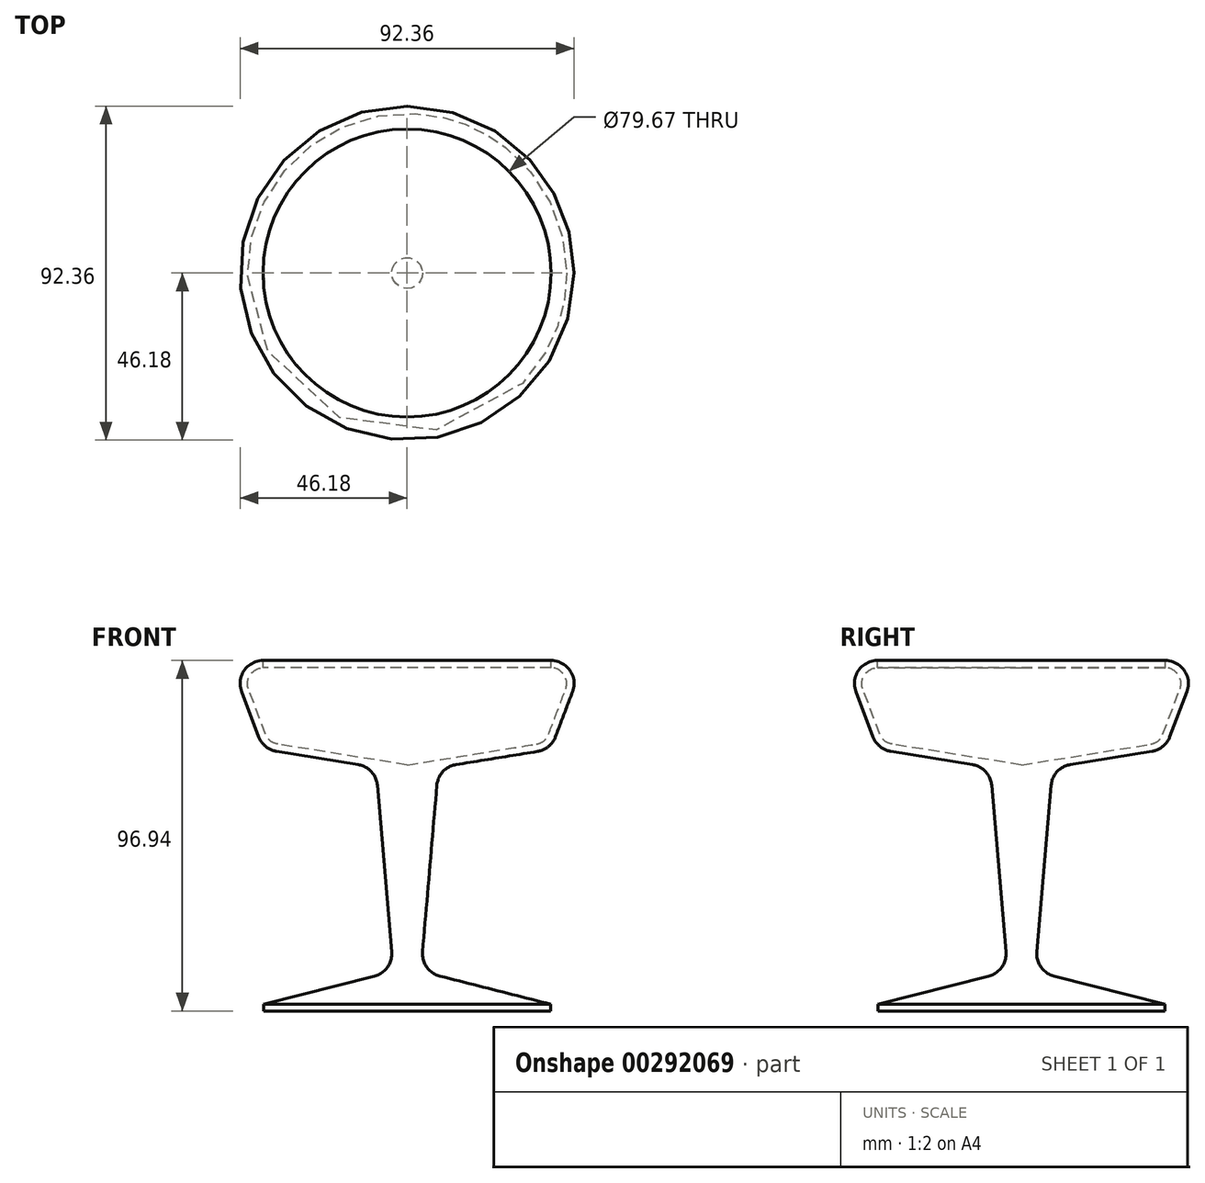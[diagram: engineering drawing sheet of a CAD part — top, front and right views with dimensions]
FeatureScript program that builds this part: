
annotation { "Feature Type Name" : "Feature", "Feature Type Description" : "" }
export const myFeature = defineFeature(function(context is Context, id is Id, definition is map)
    precondition{}
    {
        {
            var Q0;
            Q0=qCreatedBy(makeId("Right.planeOp"),FACE);
            var sketch = newSketch(context, id + "F0", { "sketchPlane" : qUnion([Q0])});
            skLineSegment(sketch, "E0", {"start": v(0, -50.24) * mm, "end": v(-39.73, -50.24) * mm});
            skLineSegment(sketch, "E1", {"start": v(-39.73, -50.24) * mm, "end": v(-39.73, -48.38) * mm});
            skLineSegment(sketch, "E2", {"start": v(-39.73, -48.38) * mm, "end": v(-9.04, -40.59) * mm});
            skLineSegment(sketch, "E3", {"start": v(-4.28, -33.89) * mm, "end": v(-8.23, 12.18) * mm});
            skLineSegment(sketch, "E4", {"start": v(-13.54, 17.9) * mm, "end": v(-36.1, 21.56) * mm});
            skLineSegment(sketch, "E5", {"start": v(-41.03, 25.58) * mm, "end": v(-45.77, 38.1) * mm});
            skLineSegment(sketch, "E6", {"start": v(0, 46.7) * mm, "end": v(0, -50.24) * mm});
            skPoint(sketch, "E7.visualSharp", {"position": v(-49.03, 46.7) * mm});
            skArc(sketch, "E7.filletArc", {"start": v(-39.83, 46.7) * mm, "mid": v(-45.06, 43.96) * mm, "end": v(-45.77, 38.1) * mm});
            skPoint(sketch, "E8.visualSharp", {"position": v(-39.73, 22.14) * mm});
            skArc(sketch, "E8.filletArc", {"start": v(-41.03, 25.58) * mm, "mid": v(-39.1, 22.9) * mm, "end": v(-36.1, 21.56) * mm});
            skPoint(sketch, "E9.visualSharp", {"position": v(-8.65, 17.12) * mm});
            skArc(sketch, "E9.filletArc", {"start": v(-8.23, 12.18) * mm, "mid": v(-9.9, 15.96) * mm, "end": v(-13.54, 17.9) * mm});
            skPoint(sketch, "E10.visualSharp", {"position": v(-3.81, -39.26) * mm});
            skArc(sketch, "E10.filletArc", {"start": v(-9.04, -40.59) * mm, "mid": v(-5.43, -38.11) * mm, "end": v(-4.28, -33.89) * mm});
            skArc(sketch, "E11.0", {"start": v(-39.13, 26.3) * mm, "mid": v(-37.82, 24.48) * mm, "end": v(-35.78, 23.56) * mm});
            skLineSegment(sketch, "E11.1", {"start": v(-39.13, 26.3) * mm, "end": v(-43.87, 38.82) * mm});
            skArc(sketch, "E11.2", {"start": v(-39.83, 44.67) * mm, "mid": v(-43.39, 42.8) * mm, "end": v(-43.87, 38.82) * mm});
            skLineSegment(sketch, "E12", {"start": v(-35.78, 23.56) * mm, "end": v(0, 17.78) * mm});
            skLineSegment(sketch, "E13", {"start": v(-39.83, 44.67) * mm, "end": v(-39.83, 46.7) * mm});
            skSolve(sketch);
        }
        {
            var Q0;
            {var subQ1=sQuery(id+"F0.wireOp",EDGE,"E0");Q0=makeQuery(id+"F0.imprint","IMPRINT",FACE,{"disambiguationData":[TD([[makeQuery(id+"F0.imprint","IMPRINT",EDGE,{"derivedFrom":subQ1}),-1.0]])]});}
            var Q1;
            Q1=sQuery(id+"F0.wireOp",EDGE,"E6");
            revolve(context, id + "F1", {"entities" : qUnion([Q0]), "axis" : qUnion([Q1]), "revolveType" : RevolveType.FULL});
        }
    });
